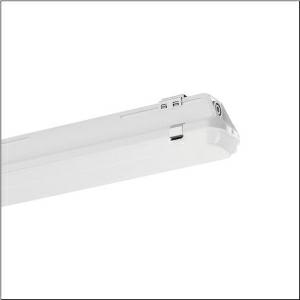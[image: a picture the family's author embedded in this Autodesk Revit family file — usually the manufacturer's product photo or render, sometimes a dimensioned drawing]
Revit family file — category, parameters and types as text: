
# Revit family: monsun_r__21_emergency_51fb20dp467c3h_1d79
name_source: partatom
category: Lighting Fixtures
units: mm (PartAtom-declared; Revit-internal decimal feet)

## family parameters
Cut with Voids When Loaded = No
Host = Face
Light Source = No
Part Type = Normal
Room Calculation Point = No
Round Connector Dimension = Use Diameter
Shared = No

## types (1)
- --- (1 x LED, 5460 lm, 36.5 W, 4000K)
    Apparent Load = 37 VA
    CIE Flux Codes = 45 75 93 94 100
    Color Rendering = 80
    Color Temperature = 4000K
    Default Elevation = 1800 mm
    Description = Monsun® 21 emergency, damp-proof luminaire, chain hanger, primary optical cover: enclosure, of PC, light emission: direct distribution, primary light characteristic: symmetric, installation type: vertical mounting, horizontal mounting, surface-mounted, suspended mounting, LED, rated luminous flux: 5.460lm, luminous efficacy: 167lm/W, light colour: 840, colour temperature: 4000K, control gear: DALI 2, with terminal, 5+3-pole, max. 2.5mm², mains connection: 220..240V, AC, 50/60Hz, rated input power: 37W, control gear: single battery element, battery: LiFePO4, 9Ah, housing, of glass-fibre reinforced polyester, uncoated, bright grey, incl. chain hanger, length: 1.590mm, width: 90mm, height: 88mm, clip for enclosure, of stainless steel (V2A), ceiling mounting element, of stainless steel (V2A), chain hanger, of stainless steel (V2A), protection rating (complete): IP66, insulation class (complete): insulation class I (protective earthing), certification: CE, UKCA, protection symbol: D, impact resistance: IK08, permissible operating ambient temperature: +5..+25°C, standard: EN 50419, EN 60598-2-1, EN 60598-2-22, corresponds to IFS (International Featured Standards) requirements for safety and quality in the food industry, for indoor or canopied outdoor use, no direct snow, no direct sun, no direct rain, LABS conformity tested according to VDMA 24364:2018-05, contact your sales advisor before using the luminaires in applications with unclear chemical exposure, large temperature fluctuations or condensation-forming humidity, packaging unit: 1 piece
    Height = 89 mm
    Lamp = 1 x LED
    Lamp Light Flux = 5460 lm
    Lamp Power = 36.5 W
    Lamp count = 1
    Length = 1590 mm
    Luminous efficacy = 150 lm/W
    Manufacturer = Siteco
    ModVariant = No
    Model = 51FB20DP467C3H
    Mounting Place = Ceiling
    Mounting Type = Surface mounted
    Number of Poles = 1
    OnlyDefault = Yes
    Power Factor = 1
    Product Name = Monsun® 21 emergency
    Product group = damp-proof luminaire
    ProductGroupID = 300
    Protection Class = Protection class I
    Protection Degree = IP 66
    RLX_Detail_Level = 1
    RLX_Emergency_Light_Flux = 0 lm
    RLX_Emergency_Type = 0
    RLX_Emergency_Type_DB = No
    RlxData = <blob elided: 92169 chars, md5=dfaf9aae>
    Socket = socket
    Standby Power = 0 W
    System Light Flux = 5460 lm
    System Power = 37 W
    Type Comments = : luminous flux: 100 % | dim-lin: 254 | 229 mA
    Type Image = l_1319656.jpg
    URL = http://relux.com
    VarID = @adj_041838
    Voltage = 0 V
    Weight = 0.00 kg
    Width = 90 mm

## geometry (parser evidence)
native form markers: Blend x4, Sweep x13
no freeform markers — native parametric forms only
